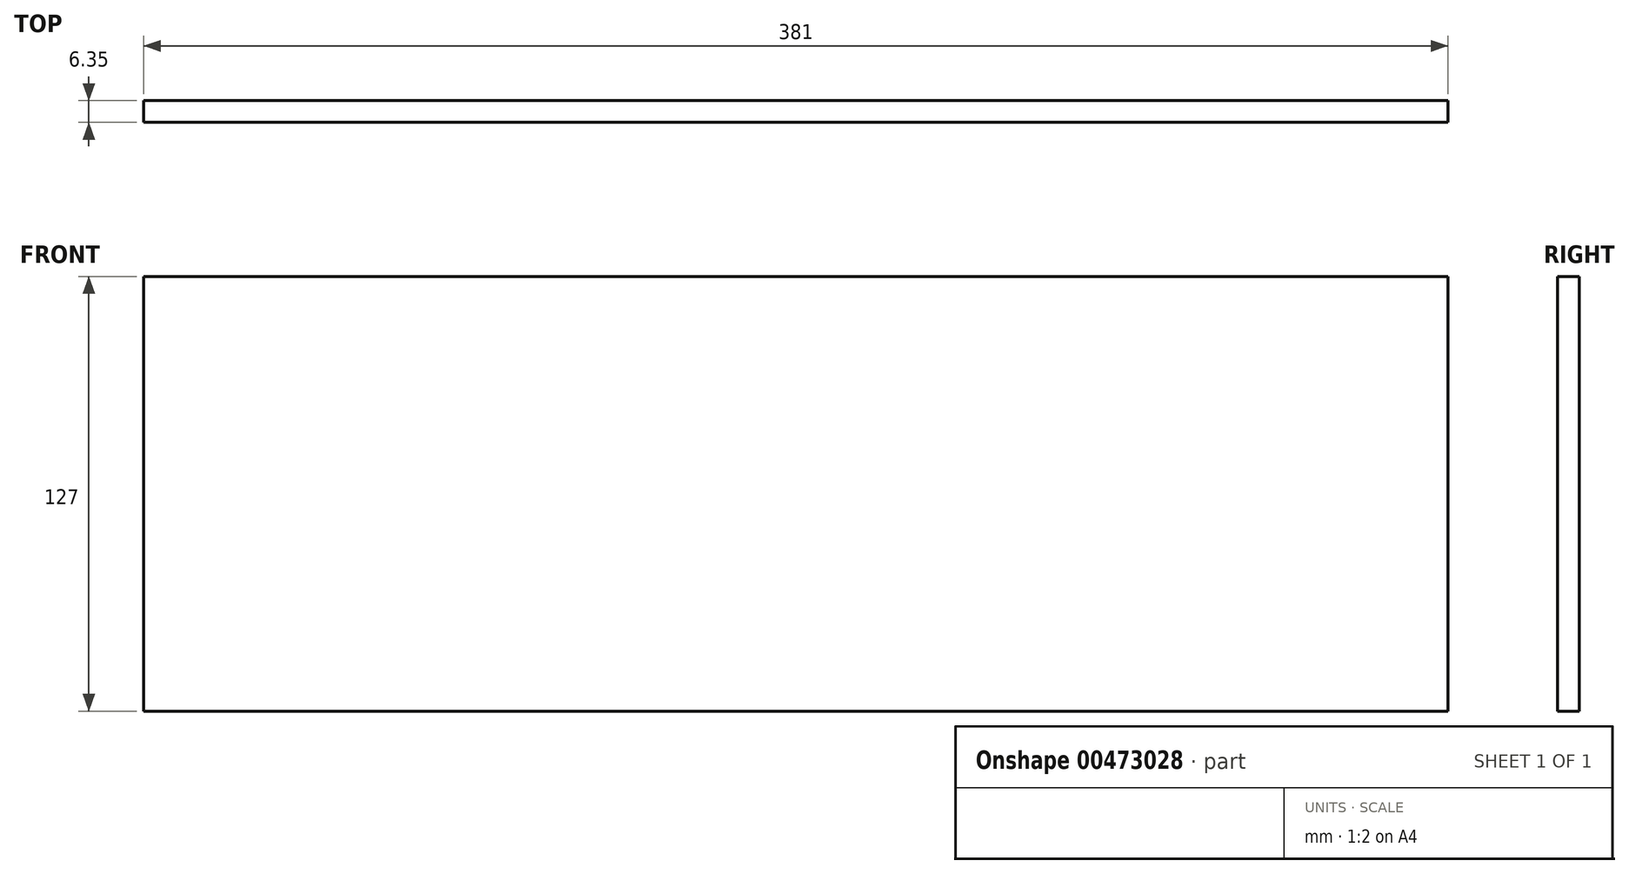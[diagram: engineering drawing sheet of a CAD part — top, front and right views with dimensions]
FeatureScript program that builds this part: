
annotation { "Feature Type Name" : "Feature", "Feature Type Description" : "" }
export const myFeature = defineFeature(function(context is Context, id is Id, definition is map)
    precondition{}
    {
        {
            var Q0;
            Q0=qCreatedBy(makeId("Front.planeOp"),FACE);
            var sketch = newSketch(context, id + "F0", { "sketchPlane" : qUnion([Q0])});
            skLineSegment(sketch, "E0.bottom", {"start": v(190.5, 63.5) * mm, "end": v(-190.5, 63.5) * mm});
            skLineSegment(sketch, "E0.top", {"start": v(190.5, -63.5) * mm, "end": v(-190.5, -63.5) * mm});
            skLineSegment(sketch, "E0.left", {"start": v(190.5, 63.5) * mm, "end": v(190.5, -63.5) * mm});
            skLineSegment(sketch, "E0.right", {"start": v(-190.5, 63.5) * mm, "end": v(-190.5, -63.5) * mm});
            skPoint(sketch, "E0.middle", {"position": v(0, 0) * mm});
            skSolve(sketch);
        }
        {
            var Q0;
            Q0=makeQuery(id+"F0.imprint","IMPRINT",FACE,{"disambiguationData":[TD([[makeQuery(id+"F0.imprint","IMPRINT",EDGE,{"derivedFrom":sQuery(id+"F0.wireOp",EDGE,"E0.bottom")}),1.0]])]});
            extrude(context, id + "F1", {"entities" : qUnion([Q0]), "depth" : 6.35 * mm});
        }
    });
